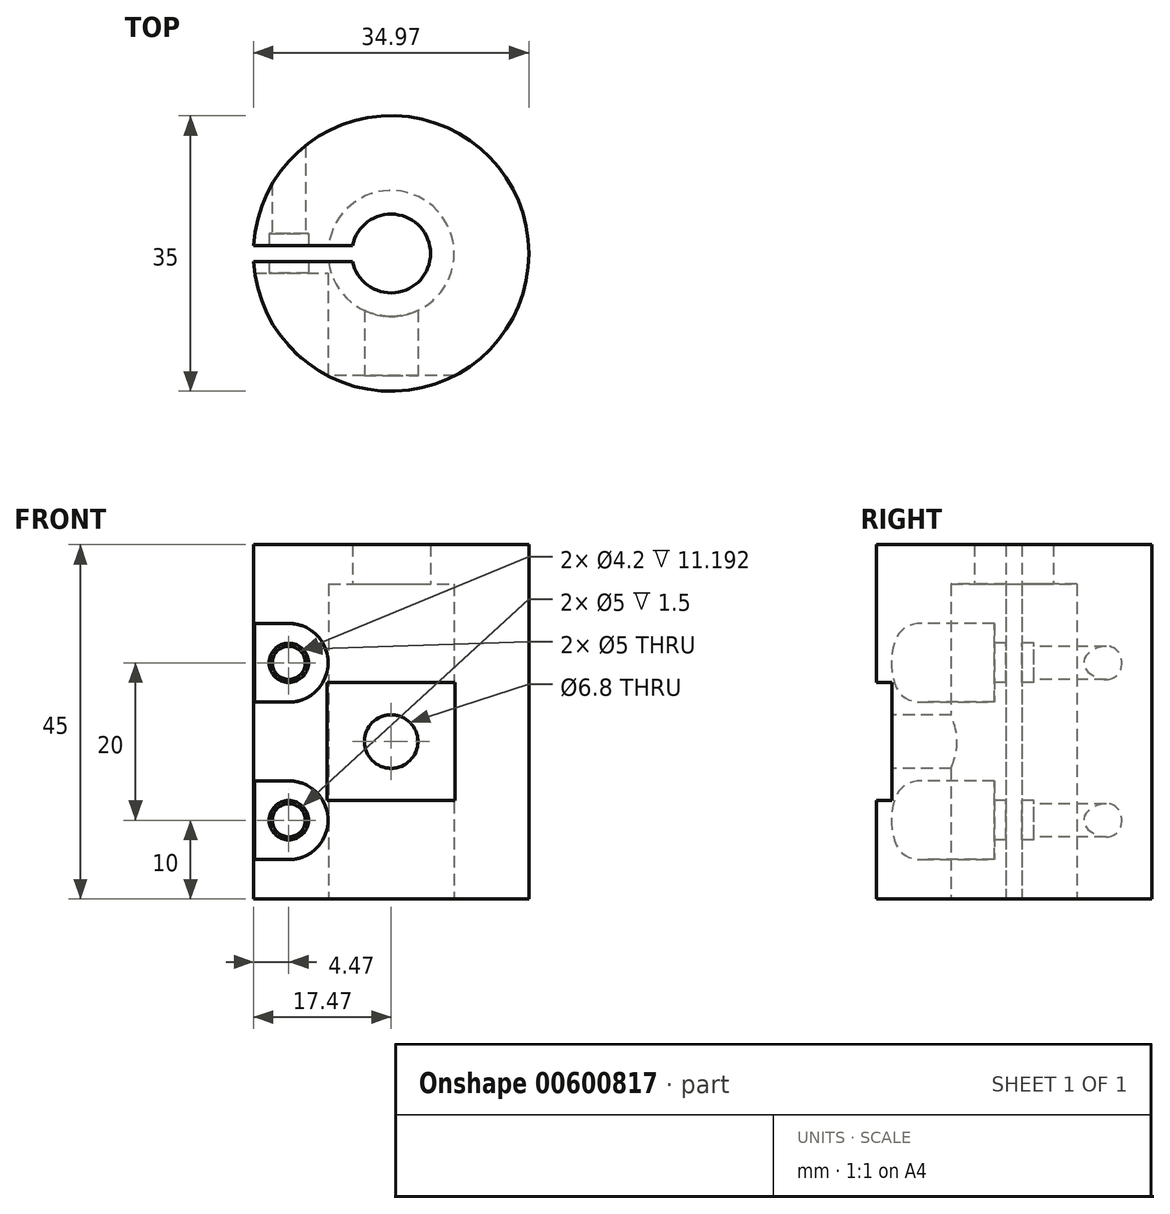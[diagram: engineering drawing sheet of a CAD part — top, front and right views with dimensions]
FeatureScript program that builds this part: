
annotation { "Feature Type Name" : "Feature", "Feature Type Description" : "" }
export const myFeature = defineFeature(function(context is Context, id is Id, definition is map)
    precondition{}
    {
        {
            var Q0;
            Q0=qCreatedBy(makeId("Top.planeOp"),FACE);
            var sketch = newSketch(context, id + "F0", { "sketchPlane" : qUnion([Q0])});
            skCircle(sketch, "E0", {"center": v(0, 0) * mm, "radius": 17.5 * mm});
            skCircle(sketch, "E1", {"center": v(0, 0) * mm, "radius": 8 * mm});
            skSolve(sketch);
        }
        {
            var Q0;
            Q0 = qSketchRegion(id + "F0", true);
            extrude(context, id + "F1", {"entities" : qUnion([Q0]), "depth" : 40 * mm, "offsetDistance" : 25 * mm});
        }
        {
            var Q0;
            Q0=qCreatedBy(makeId("Front.planeOp"),FACE);
            cPlane(context, id + "F2", {"entities" : qUnion([Q0]), "cplaneType" : CPlaneType.OFFSET, "offset" : 17.5 * mm, "width" : 150 * mm, "height" : 150 * mm});
        }
        {
            var Q0;
            Q0=qCreatedBy(id+"F2.planeOp",FACE);
            var sketch = newSketch(context, id + "F3", { "sketchPlane" : qUnion([Q0])});
            skLineSegment(sketch, "E2", {"start": v(-13, 0) * mm, "end": v(-13, 52.55) * mm, "construction": true});
            skArc(sketch, "E3", {"start": v(-13, 5) * mm, "mid": v(-8, 10) * mm, "end": v(-13, 15) * mm});
            skArc(sketch, "E4", {"start": v(-13, 25) * mm, "mid": v(-8, 30) * mm, "end": v(-13, 35) * mm});
            skLineSegment(sketch, "E5", {"start": v(-18, 0) * mm, "end": v(-18, 45.32) * mm, "construction": true});
            skLineSegment(sketch, "E6", {"start": v(-13, 35) * mm, "end": v(-18, 35) * mm});
            skLineSegment(sketch, "E7", {"start": v(-18, 35) * mm, "end": v(-18, 25) * mm});
            skLineSegment(sketch, "E8", {"start": v(-18, 25) * mm, "end": v(-13, 25) * mm});
            skLineSegment(sketch, "E9", {"start": v(-13, 15) * mm, "end": v(-18, 15) * mm});
            skLineSegment(sketch, "E10", {"start": v(-18, 15) * mm, "end": v(-18, 5) * mm});
            skLineSegment(sketch, "E11", {"start": v(-18, 5) * mm, "end": v(-13, 5) * mm});
            skSolve(sketch);
        }
        {
            var Q0;
            Q0 = qSketchRegion(id + "F3", true);
            extrude(context, id + "F4", {"entities" : qUnion([Q0]), "operationType" : NewBodyOperationType.REMOVE, "oppositeDirection" : true, "depth" : 15 * mm, "offsetDistance" : 25 * mm});
        }
        {
            var Q0;
            Q0=makeQuery(id+"F1.opExtrude","CAP_FACE",FACE,{"disambiguationData":[OSD([sQuery(id+"F0.wireOp",EDGE,"E0"),sQuery(id+"F0.wireOp",EDGE,"E1")])],"isStart":true});
            var sketch = newSketch(context, id + "F5", { "sketchPlane" : qUnion([Q0])});
            skLineSegment(sketch, "E12.bottom", {"start": v(0, 1) * mm, "end": v(-20, 1) * mm});
            skLineSegment(sketch, "E12.top", {"start": v(0, -1) * mm, "end": v(-20, -1) * mm});
            skLineSegment(sketch, "E12.left", {"start": v(0, 1) * mm, "end": v(0, -1) * mm});
            skLineSegment(sketch, "E12.right", {"start": v(-20, 1) * mm, "end": v(-20, -1) * mm});
            skSolve(sketch);
        }
        {
            var Q0;
            Q0=makeQuery(id+"F1.opExtrude","CAP_FACE",FACE,{"disambiguationData":[OSD([sQuery(id+"F0.wireOp",EDGE,"E0"),sQuery(id+"F0.wireOp",EDGE,"E1")])],"isStart":false});
            var sketch = newSketch(context, id + "F6", { "sketchPlane" : qUnion([Q0])});
            skCircle(sketch, "E13", {"center": v(0, 0) * mm, "radius": 17.5 * mm});
            skCircle(sketch, "E14", {"center": v(0, 0) * mm, "radius": 5 * mm});
            skSolve(sketch);
        }
        {
            var Q0;
            Q0 = qSketchRegion(id + "F6", true);
            extrude(context, id + "F7", {"entities" : qUnion([Q0]), "operationType" : NewBodyOperationType.ADD, "depth" : 5 * mm, "offsetDistance" : 25 * mm});
        }
        {
            var Q0;
            Q0 = qSketchRegion(id + "F5", true);
            extrude(context, id + "F8", {"entities" : qUnion([Q0]), "operationType" : NewBodyOperationType.REMOVE, "endBound" : BoundingType.THROUGH_ALL, "oppositeDirection" : true, "depth" : 25 * mm, "offsetDistance" : 25 * mm});
        }
        {
            var Q0;
            Q0=qCreatedBy(id+"F2.planeOp",FACE);
            var sketch = newSketch(context, id + "F9", { "sketchPlane" : qUnion([Q0])});
            skCircle(sketch, "E15", {"center": v(0, 20) * mm, "radius": 3.4 * mm});
            skSolve(sketch);
        }
        {
            var Q0;
            Q0 = qSketchRegion(id + "F9", true);
            extrude(context, id + "F10", {"entities" : qUnion([Q0]), "operationType" : NewBodyOperationType.REMOVE, "oppositeDirection" : true, "depth" : 20 * mm, "offsetDistance" : 25 * mm});
        }
        {
            var Q0;
            Q0=qCreatedBy(id+"F2.planeOp",FACE);
            var sketch = newSketch(context, id + "F11", { "sketchPlane" : qUnion([Q0])});
            skLineSegment(sketch, "E16.bottom", {"start": v(10, 27.5) * mm, "end": v(-10, 27.5) * mm});
            skLineSegment(sketch, "E16.top", {"start": v(10, 12.5) * mm, "end": v(-10, 12.5) * mm});
            skLineSegment(sketch, "E16.left", {"start": v(10, 27.5) * mm, "end": v(10, 12.5) * mm});
            skLineSegment(sketch, "E16.right", {"start": v(-10, 27.5) * mm, "end": v(-10, 12.5) * mm});
            skPoint(sketch, "E16.middle", {"position": v(0, 20) * mm});
            skSolve(sketch);
        }
        {
            var Q0;
            Q0 = qSketchRegion(id + "F11", true);
            extrude(context, id + "F12", {"entities" : qUnion([Q0]), "operationType" : NewBodyOperationType.REMOVE, "oppositeDirection" : true, "depth" : 2 * mm, "offsetDistance" : 25 * mm});
        }
        {
            var Q0;
            Q0=makeQuery(id+"F4.boolean.opBoolean","COPY",FACE,{"derivedFrom":makeQuery(id+"F4.opExtrude","CAP_FACE",FACE,{"disambiguationData":[OSD([sQuery(id+"F3.wireOp",EDGE,"E4"),sQuery(id+"F3.wireOp",EDGE,"E6"),sQuery(id+"F3.wireOp",EDGE,"E7"),sQuery(id+"F3.wireOp",EDGE,"E8")])],"isStart":false})});
            var sketch = newSketch(context, id + "F13", { "sketchPlane" : qUnion([Q0])});
            skCircle(sketch, "E17", {"center": v(-13, 30) * mm, "radius": 2.1 * mm});
            skCircle(sketch, "E18", {"center": v(-13, 30) * mm, "radius": 2.5 * mm});
            skSolve(sketch);
        }
        {
            var Q0;
            Q0=makeQuery(id+"F13.imprint","IMPRINT",FACE,{"disambiguationData":[TD([[makeQuery(id+"F13.imprint","IMPRINT",EDGE,{"derivedFrom":sQuery(id+"F13.wireOp",EDGE,"E17")}),1.0]])]});
            extrude(context, id + "F14", {"entities" : qUnion([Q0]), "operationType" : NewBodyOperationType.REMOVE, "oppositeDirection" : true, "depth" : 25 * mm, "offsetDistance" : 25 * mm});
        }
        {
            var Q0;
            Q0 = qSketchRegion(id + "F13", true);
            extrude(context, id + "F15", {"entities" : qUnion([Q0]), "operationType" : NewBodyOperationType.REMOVE, "oppositeDirection" : true, "depth" : 5 * mm, "offsetDistance" : 25 * mm});
        }
        {
            var Q0;
            Q0=makeQuery(id+"F4.boolean.opBoolean","COPY",FACE,{"derivedFrom":makeQuery(id+"F4.opExtrude","CAP_FACE",FACE,{"disambiguationData":[OSD([sQuery(id+"F3.wireOp",EDGE,"E3"),sQuery(id+"F3.wireOp",EDGE,"E9"),sQuery(id+"F3.wireOp",EDGE,"E10"),sQuery(id+"F3.wireOp",EDGE,"E11")])],"isStart":false})});
            var sketch = newSketch(context, id + "F16", { "sketchPlane" : qUnion([Q0])});
            skCircle(sketch, "E19", {"center": v(-13, 10) * mm, "radius": 2.1 * mm});
            skSolve(sketch);
        }
        {
            var Q0;
            Q0 = qSketchRegion(id + "F16", true);
            extrude(context, id + "F17", {"entities" : qUnion([Q0]), "operationType" : NewBodyOperationType.REMOVE, "oppositeDirection" : true, "depth" : 25 * mm, "offsetDistance" : 25 * mm});
        }
        {
            var Q0;
            Q0=makeQuery(id+"F4.boolean.opBoolean","COPY",FACE,{"derivedFrom":makeQuery(id+"F4.opExtrude","CAP_FACE",FACE,{"disambiguationData":[OSD([sQuery(id+"F3.wireOp",EDGE,"E3"),sQuery(id+"F3.wireOp",EDGE,"E9"),sQuery(id+"F3.wireOp",EDGE,"E10"),sQuery(id+"F3.wireOp",EDGE,"E11")])],"isStart":false})});
            var sketch = newSketch(context, id + "F18", { "sketchPlane" : qUnion([Q0])});
            skCircle(sketch, "E20", {"center": v(-13, 10) * mm, "radius": 2.5 * mm});
            skSolve(sketch);
        }
        {
            var Q0;
            Q0 = qSketchRegion(id + "F18", true);
            extrude(context, id + "F19", {"entities" : qUnion([Q0]), "operationType" : NewBodyOperationType.REMOVE, "oppositeDirection" : true, "depth" : 5 * mm, "offsetDistance" : 25 * mm});
        }
    });
